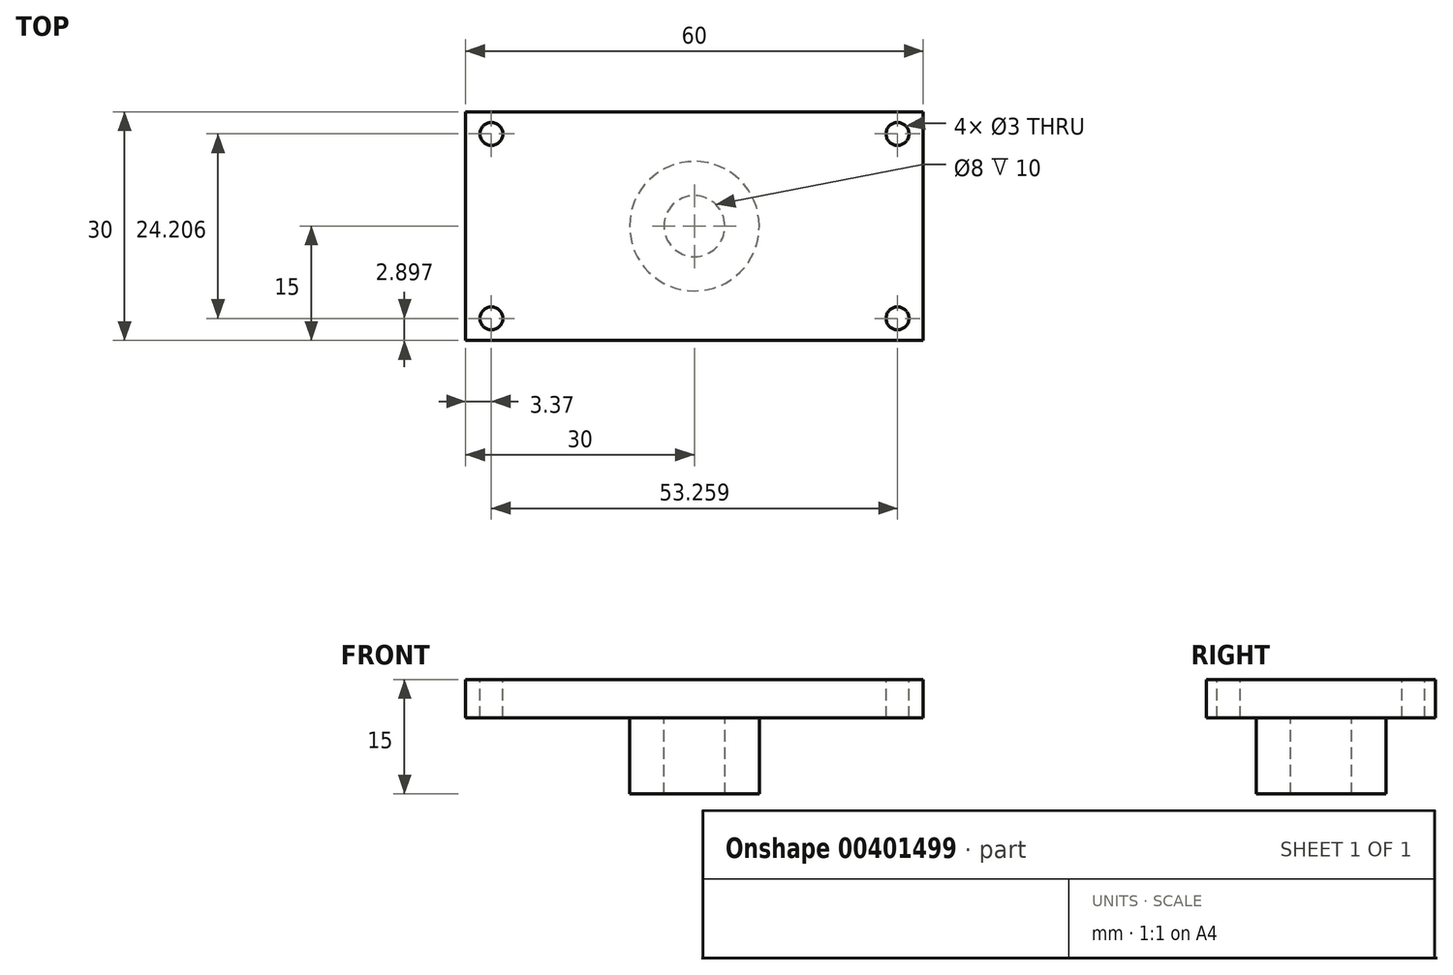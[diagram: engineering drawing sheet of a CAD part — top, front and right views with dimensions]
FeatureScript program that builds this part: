
annotation { "Feature Type Name" : "Feature", "Feature Type Description" : "" }
export const myFeature = defineFeature(function(context is Context, id is Id, definition is map)
    precondition{}
    {
        {
            var Q0;
            Q0=qCreatedBy(makeId("Top.planeOp"),FACE);
            var sketch = newSketch(context, id + "F0", { "sketchPlane" : qUnion([Q0])});
            skLineSegment(sketch, "E0.bottom", {"start": v(-30, 15) * mm, "end": v(30, 15) * mm});
            skLineSegment(sketch, "E0.top", {"start": v(-30, -15) * mm, "end": v(30, -15) * mm});
            skLineSegment(sketch, "E0.left", {"start": v(-30, 15) * mm, "end": v(-30, -15) * mm});
            skLineSegment(sketch, "E0.right", {"start": v(30, 15) * mm, "end": v(30, -15) * mm});
            skPoint(sketch, "E0.middle", {"position": v(0, 0) * mm});
            skSolve(sketch);
        }
        {
            var Q0;
            Q0=makeQuery(id+"F0.imprint","IMPRINT",FACE,{"disambiguationData":[TD([[makeQuery(id+"F0.imprint","IMPRINT",EDGE,{"derivedFrom":sQuery(id+"F0.wireOp",EDGE,"E0.bottom")}),-1.0]])]});
            var sketch = newSketch(context, id + "F1", { "sketchPlane" : qUnion([Q0])});
            skCircle(sketch, "E1", {"center": v(0, 0) * mm, "radius": 8.5 * mm});
            skCircle(sketch, "E2", {"center": v(0, 0) * mm, "radius": 4 * mm});
            skSolve(sketch);
        }
        {
            var Q0;
            Q0=makeQuery(id+"F0.imprint","IMPRINT",FACE,{"disambiguationData":[TD([[makeQuery(id+"F0.imprint","IMPRINT",EDGE,{"derivedFrom":sQuery(id+"F0.wireOp",EDGE,"E0.bottom")}),-1.0]])]});
            var sketch = newSketch(context, id + "F2", { "sketchPlane" : qUnion([Q0])});
            skCircle(sketch, "E3", {"center": v(-26.63, -12.1) * mm, "radius": 1.5 * mm});
            skCircle(sketch, "E4.MirrorC", {"center": v(-26.63, 12.1) * mm, "radius": 1.5 * mm});
            skCircle(sketch, "E5.MirrorC", {"center": v(26.63, -12.1) * mm, "radius": 1.5 * mm});
            skCircle(sketch, "E6.MirrorC", {"center": v(26.63, 12.1) * mm, "radius": 1.5 * mm});
            skSolve(sketch);
        }
        {
            var Q0;
            Q0=makeQuery(id+"F2.imprint","IMPRINT",FACE,{"disambiguationData":[TD([[makeQuery(id+"F2.imprint","IMPRINT",EDGE,{"derivedFrom":sQuery(id+"F2.wireOp",EDGE,"E3")}),-1.0]])]});
            extrude(context, id + "F3", {"entities" : qUnion([Q0]), "oppositeDirection" : true, "depth" : 5 * mm});
        }
        {
            var Q0;
            Q0=makeQuery(id+"F1.imprint","IMPRINT",FACE,{"disambiguationData":[TD([[makeQuery(id+"F1.imprint","IMPRINT",EDGE,{"derivedFrom":sQuery(id+"F1.wireOp",EDGE,"E1")}),1.0]])]});
            extrude(context, id + "F4", {"entities" : qUnion([Q0]), "operationType" : NewBodyOperationType.ADD, "oppositeDirection" : true, "depth" : 15 * mm});
        }
    });
